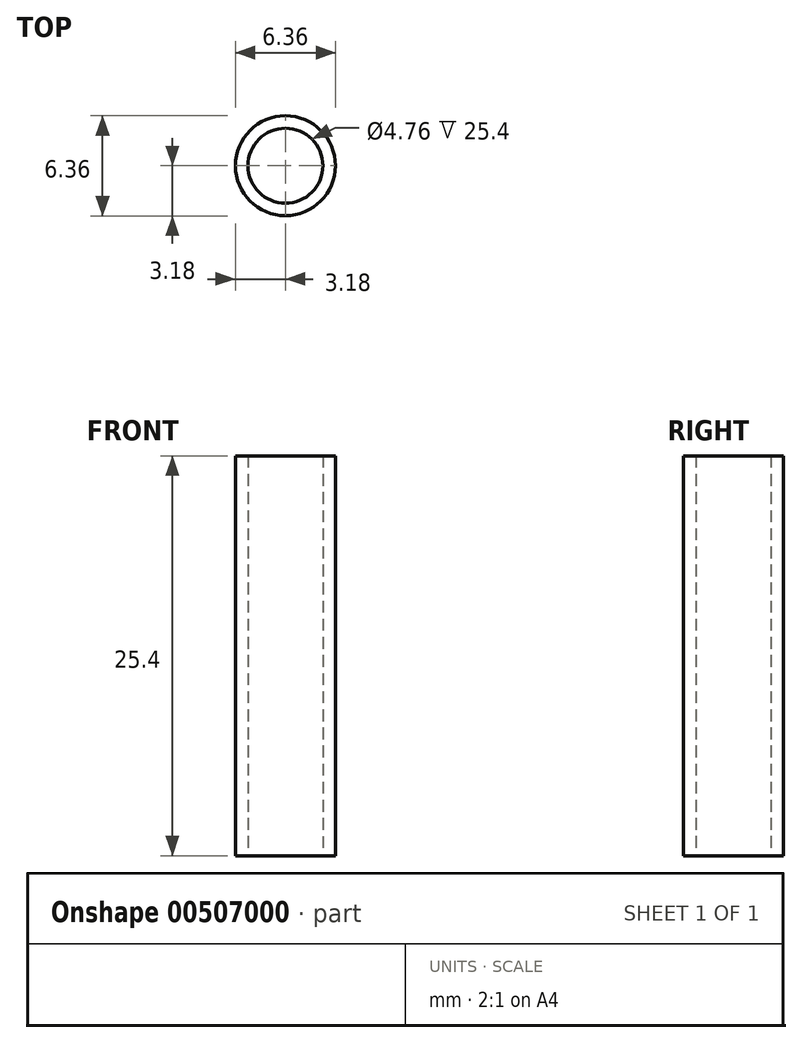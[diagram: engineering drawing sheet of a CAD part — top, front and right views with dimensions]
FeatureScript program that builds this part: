
annotation { "Feature Type Name" : "Feature", "Feature Type Description" : "" }
export const myFeature = defineFeature(function(context is Context, id is Id, definition is map)
    precondition{}
    {
        {
            var Q0;
            Q0=qCreatedBy(makeId("Top.planeOp"),FACE);
            var sketch = newSketch(context, id + "F0", { "sketchPlane" : qUnion([Q0])});
            skCircle(sketch, "E0", {"center": v(0, 0) * mm, "radius": 3.18 * mm});
            skCircle(sketch, "E1", {"center": v(0, 0) * mm, "radius": 2.38 * mm});
            skSolve(sketch);
        }
        {
            var Q0;
            Q0 = qSketchRegion(id + "F0", true);
            extrude(context, id + "F1", {"entities" : qUnion([Q0]), "depth" : 25.4 * mm});
        }
    });
